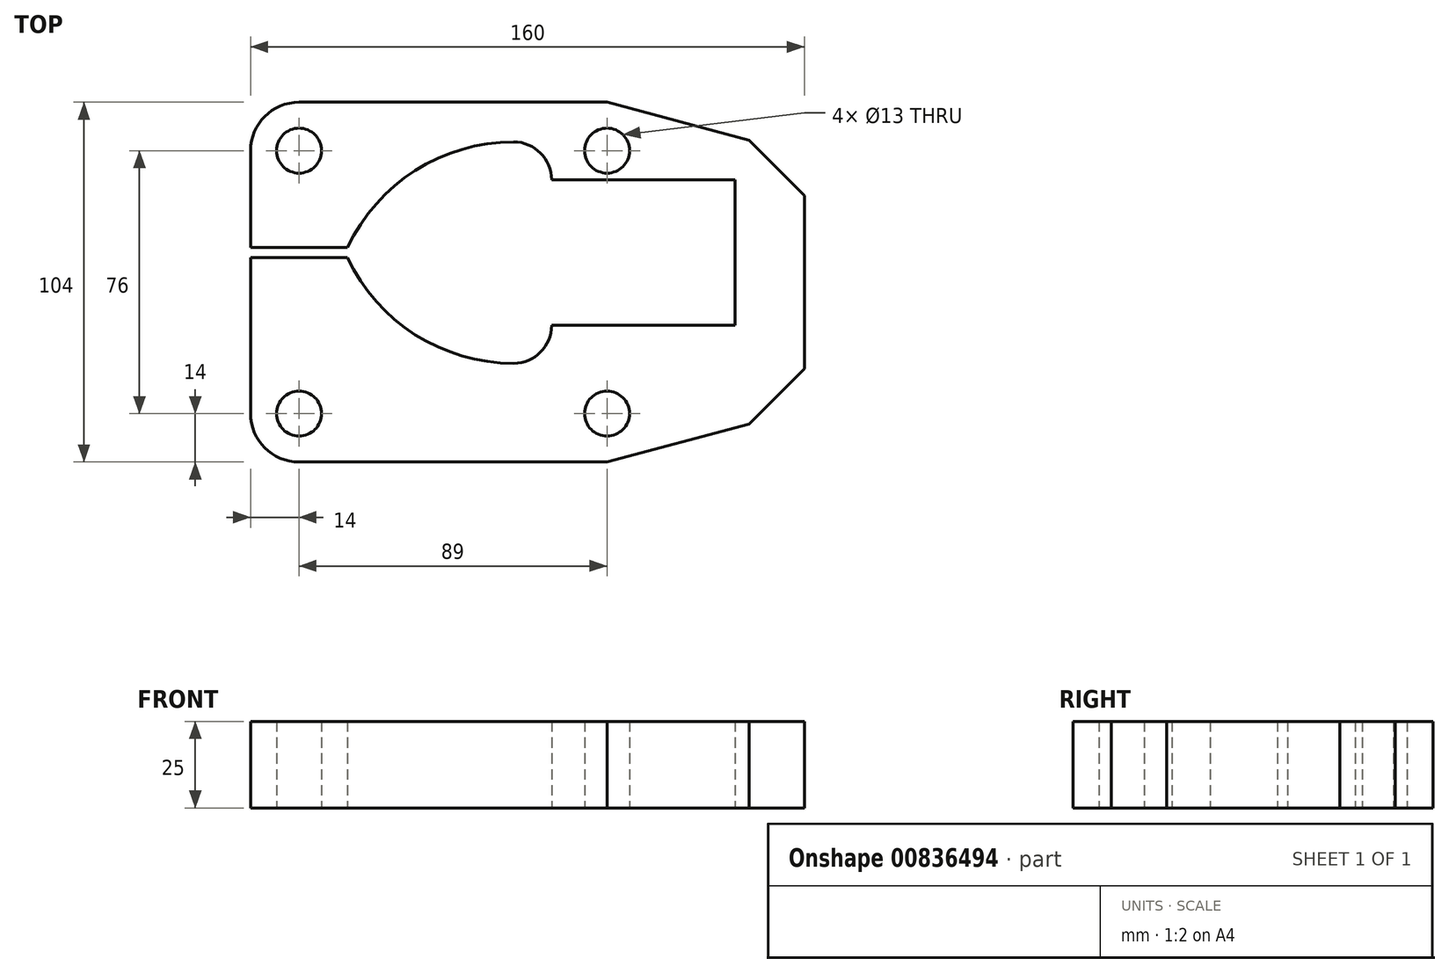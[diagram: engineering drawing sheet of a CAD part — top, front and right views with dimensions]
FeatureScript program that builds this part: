
annotation { "Feature Type Name" : "Feature", "Feature Type Description" : "" }
export const myFeature = defineFeature(function(context is Context, id is Id, definition is map)
    precondition{}
    {
        {
            var Q0;
            Q0=qCreatedBy(makeId("Top.planeOp"),FACE);
            var sketch = newSketch(context, id + "F0", { "sketchPlane" : qUnion([Q0])});
            skCircle(sketch, "E0", {"center": v(-89, 0) * mm, "radius": 6.5 * mm});
            skCircle(sketch, "E1", {"center": v(0, 0) * mm, "radius": 6.5 * mm});
            skCircle(sketch, "E2", {"center": v(-89, -76) * mm, "radius": 6.5 * mm});
            skCircle(sketch, "E3", {"center": v(0, -76) * mm, "radius": 6.5 * mm});
            skLineSegment(sketch, "E4", {"start": v(0, 0) * mm, "end": v(0, -8.48) * mm, "construction": true});
            skArc(sketch, "E5", {"start": v(-103, -76) * mm, "mid": v(-79.1, -85.9) * mm, "end": v(-89, -62) * mm});
            skArc(sketch, "E6", {"start": v(-89, 14) * mm, "mid": v(-98.9, 9.9) * mm, "end": v(-103, 0) * mm});
            skLineSegment(sketch, "E7.bottom", {"start": v(-89, -76) * mm, "end": v(-103, -76) * mm});
            skLineSegment(sketch, "E7.top", {"start": v(-89, -30.95) * mm, "end": v(-103, -30.95) * mm});
            skLineSegment(sketch, "E7.left", {"start": v(-89, -76) * mm, "end": v(-89, -30.95) * mm});
            skLineSegment(sketch, "E7.right", {"start": v(-103, -76) * mm, "end": v(-103, -30.95) * mm});
            skLineSegment(sketch, "E8", {"start": v(-89, -90) * mm, "end": v(0, -90) * mm});
            skLineSegment(sketch, "E9", {"start": v(-89, 14) * mm, "end": v(0, 14) * mm});
            skPoint(sketch, "E9.endSnap0", {"position": v(0, -38) * mm});
            skLineSegment(sketch, "E10", {"start": v(-89, -38) * mm, "end": v(0, -38) * mm, "construction": true});
            skLineSegment(sketch, "E11.bottom", {"start": v(0, -38) * mm, "end": v(37, -38) * mm});
            skLineSegment(sketch, "E11.top", {"start": v(0, -8.48) * mm, "end": v(37, -8.48) * mm});
            skLineSegment(sketch, "E11.right", {"start": v(37, -38) * mm, "end": v(37, -8.48) * mm});
            skLineSegment(sketch, "E12.top", {"start": v(0, -50.48) * mm, "end": v(37, -50.48) * mm});
            skLineSegment(sketch, "E12.right", {"start": v(37, -38) * mm, "end": v(37, -50.48) * mm});
            skLineSegment(sketch, "E13.trimOffspring", {"start": v(0, -50.48) * mm, "end": v(0, -76) * mm, "construction": true});
            skLineSegment(sketch, "E14", {"start": v(57, -12.99) * mm, "end": v(57, -63.01) * mm});
            skLineSegment(sketch, "E15.bottom", {"start": v(-89, 0) * mm, "end": v(-103, 0) * mm});
            skLineSegment(sketch, "E15.top", {"start": v(-89, -28) * mm, "end": v(-103, -28) * mm});
            skLineSegment(sketch, "E15.left", {"start": v(-89, 0) * mm, "end": v(-89, -28) * mm, "construction": true});
            skLineSegment(sketch, "E15.right", {"start": v(-103, 0) * mm, "end": v(-103, -28) * mm});
            skLineSegment(sketch, "E16.bottom", {"start": v(-89, 0) * mm, "end": v(-75, 0) * mm});
            skLineSegment(sketch, "E16.top", {"start": v(-89, -28) * mm, "end": v(-75, -28) * mm});
            skLineSegment(sketch, "E16.left", {"start": v(-89, 0) * mm, "end": v(-89, -28) * mm});
            skLineSegment(sketch, "E16.right", {"start": v(-75, 0) * mm, "end": v(-75, -28) * mm});
            skLineSegment(sketch, "E17.bottom", {"start": v(-89, -76) * mm, "end": v(-75, -76) * mm});
            skLineSegment(sketch, "E17.top", {"start": v(-89, -30.95) * mm, "end": v(-75, -30.95) * mm});
            skLineSegment(sketch, "E17.right", {"start": v(-75, -76) * mm, "end": v(-75, -30.95) * mm});
            skLineSegment(sketch, "E18.bottom", {"start": v(-89, 0) * mm, "end": v(-89, 0) * mm});
            skLineSegment(sketch, "E18.top", {"start": v(-89, 14) * mm, "end": v(-89, 14) * mm});
            skLineSegment(sketch, "E18.left", {"start": v(-89, 0) * mm, "end": v(-89, 14) * mm});
            skLineSegment(sketch, "E18.right", {"start": v(-89, 0) * mm, "end": v(-89, 14) * mm});
            skLineSegment(sketch, "E19.left", {"start": v(-89, 0) * mm, "end": v(-89, 14) * mm, "construction": true});
            skLineSegment(sketch, "E20.right", {"start": v(0, 0) * mm, "end": v(0, 14) * mm});
            skLineSegment(sketch, "E21.bottom", {"start": v(-89, -76) * mm, "end": v(-89, -76) * mm});
            skLineSegment(sketch, "E21.top", {"start": v(-89, -62) * mm, "end": v(-89, -62) * mm});
            skLineSegment(sketch, "E21.left", {"start": v(-89, -76) * mm, "end": v(-89, -62) * mm, "construction": true});
            skLineSegment(sketch, "E21.right", {"start": v(-89, -76) * mm, "end": v(-89, -62) * mm});
            skLineSegment(sketch, "E22.top", {"start": v(-89, -90) * mm, "end": v(-89, -90) * mm});
            skLineSegment(sketch, "E22.left", {"start": v(-89, -76) * mm, "end": v(-89, -90) * mm});
            skLineSegment(sketch, "E22.right", {"start": v(-89, -76) * mm, "end": v(-89, -90) * mm});
            skLineSegment(sketch, "E23.top", {"start": v(0, -90) * mm, "end": v(-89, -90) * mm});
            skLineSegment(sketch, "E23.left", {"start": v(0, -76) * mm, "end": v(0, -90) * mm});
            skLineSegment(sketch, "E23.right", {"start": v(-89, -76) * mm, "end": v(-89, -90) * mm, "construction": true});
            skArc(sketch, "E24", {"start": v(-16, -8.48) * mm, "mid": v(-19.22, -0.7) * mm, "end": v(-27, 2.52) * mm});
            skArc(sketch, "E25", {"start": v(-27, -61.48) * mm, "mid": v(-19.22, -58.26) * mm, "end": v(-16, -50.48) * mm});
            skLineSegment(sketch, "E26", {"start": v(0, -76) * mm, "end": v(41, -76) * mm, "construction": true});
            skLineSegment(sketch, "E27", {"start": v(57, -63.01) * mm, "end": v(41, -79.01) * mm});
            skLineSegment(sketch, "E28", {"start": v(0, -90) * mm, "end": v(41, -79.01) * mm});
            skLineSegment(sketch, "E29", {"start": v(0, 14) * mm, "end": v(41, 3.01) * mm});
            skLineSegment(sketch, "E30", {"start": v(0, 14) * mm, "end": v(43.76, 14) * mm, "construction": true});
            skLineSegment(sketch, "E31", {"start": v(41, 3.01) * mm, "end": v(57, -12.99) * mm});
            skLineSegment(sketch, "E32", {"start": v(0, -8.48) * mm, "end": v(-16, -8.48) * mm});
            skLineSegment(sketch, "E33", {"start": v(0, -50.48) * mm, "end": v(-16, -50.48) * mm});
            skArc(sketch, "E34", {"start": v(-27, 2.52) * mm, "mid": v(-55.44, -5.76) * mm, "end": v(-75, -28) * mm});
            skArc(sketch, "E35", {"start": v(-75, -30.95) * mm, "mid": v(-55.44, -53.2) * mm, "end": v(-27, -61.48) * mm});
            skSolve(sketch);
        }
        {
            var Q0;
            {var subQ1=sQuery(id+"F0.wireOp",EDGE,"E16.top");Q0=makeQuery(id+"F0.imprint","IMPRINT",FACE,{"disambiguationData":[TD([[makeQuery(id+"F0.imprint","IMPRINT",EDGE,{"derivedFrom":subQ1}),1.0]])]});}
            var Q1;
            Q1=makeQuery(id+"F0.imprint","IMPRINT",FACE,{"disambiguationData":[TD([[makeQuery(id+"F0.imprint","IMPRINT",EDGE,{"derivedFrom":sQuery(id+"F0.wireOp",EDGE,"E1")}),-1.0]])]});
            var Q2;
            {var subQ0=sQuery(id+"F0.wireOp",EDGE,"E21.right");var subQ1=sQuery(id+"F0.wireOp",EDGE,"E2");var subQ2=makeQuery(id+"F0.imprint","INTERSECT",VERTEX,{"derivedFrom":[subQ1,subQ0]});Q2=makeQuery(id+"F0.imprint","IMPRINT",FACE,{"disambiguationData":[TD([[makeQuery(id+"F0.imprint","IMPRINT",EDGE,{"disambiguationData":[TD([[subQ2,1.0]])],"derivedFrom":subQ1}),-1.0]])]});}
            var Q3;
            {var subQ0=sQuery(id+"F0.wireOp",EDGE,"E17.bottom");var subQ1=sQuery(id+"F0.wireOp",EDGE,"E2");var subQ2=makeQuery(id+"F0.imprint","INTERSECT",VERTEX,{"derivedFrom":[subQ1,subQ0]});Q3=makeQuery(id+"F0.imprint","IMPRINT",FACE,{"disambiguationData":[TD([[makeQuery(id+"F0.imprint","IMPRINT",EDGE,{"disambiguationData":[TD([[subQ2,1.0]])],"derivedFrom":subQ1}),-1.0]])]});}
            var Q4;
            Q4=makeQuery(id+"F0.imprint","IMPRINT",FACE,{"disambiguationData":[TD([[makeQuery(id+"F0.imprint","IMPRINT",EDGE,{"derivedFrom":sQuery(id+"F0.wireOp",EDGE,"E17.top")}),-1.0]])]});
            var Q5;
            Q5=makeQuery(id+"F0.imprint","IMPRINT",FACE,{"disambiguationData":[TD([[makeQuery(id+"F0.imprint","IMPRINT",EDGE,{"derivedFrom":sQuery(id+"F0.wireOp",EDGE,"E7.top")}),1.0]])]});
            var Q6;
            {var subQ0=sQuery(id+"F0.wireOp",EDGE,"E7.bottom");var subQ1=sQuery(id+"F0.wireOp",EDGE,"E2");var subQ2=makeQuery(id+"F0.imprint","INTERSECT",VERTEX,{"derivedFrom":[subQ1,subQ0]});Q6=makeQuery(id+"F0.imprint","IMPRINT",FACE,{"disambiguationData":[TD([[makeQuery(id+"F0.imprint","IMPRINT",EDGE,{"disambiguationData":[TD([[subQ2,-1.0]])],"derivedFrom":subQ1}),-1.0]])]});}
            var Q7;
            {var subQ1=sQuery(id+"F0.wireOp",EDGE,"E15.top");Q7=makeQuery(id+"F0.imprint","IMPRINT",FACE,{"disambiguationData":[TD([[makeQuery(id+"F0.imprint","IMPRINT",EDGE,{"derivedFrom":subQ1}),-1.0]])]});}
            var Q8;
            {var subQ5=sQuery(id+"F0.wireOp",EDGE,"E6");Q8=makeQuery(id+"F0.imprint","IMPRINT",FACE,{"disambiguationData":[TD([[makeQuery(id+"F0.imprint","IMPRINT",EDGE,{"derivedFrom":subQ5}),1.0]])]});}
            extrude(context, id + "F1", {"entities" : qUnion([Q0, Q1, Q2, Q3, Q4, Q5, Q6, Q7, Q8]), "depth" : 25 * mm, "offsetDistance" : 25 * mm});
        }
    });
